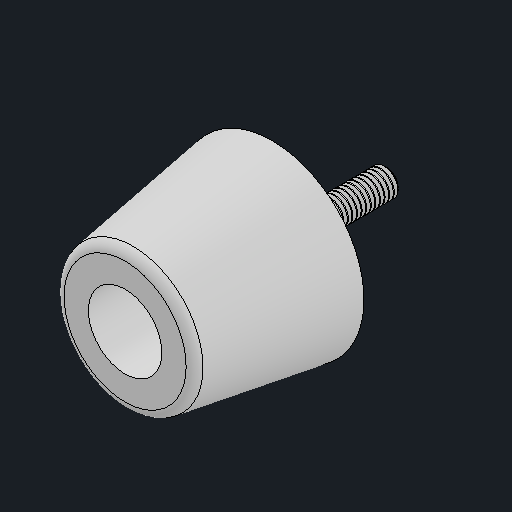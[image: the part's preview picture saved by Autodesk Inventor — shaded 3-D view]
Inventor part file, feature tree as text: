
AUTODESK INVENTOR PART (.ipt)
format: ipt  version: 2024.2 (Build 282272000, 272)  size: 256,000 bytes
history: native  units: mm
features: other x5, fillet x1
ambient origin geometry x8: Origin, YZ Plane, XZ Plane, XY Plane, X Axis, Y Axis, Z Axis, Center Point
bodies: Body1 (feature_tree), Body2 (feature_tree), Body3 (feature_tree)
feature tree (6):
  other  "솔리드1"
  other  "솔리드2"
  other  "솔리드3"
  fillet  "Fillet1"  [1 undecoded]
  other  "Boss-Extrude1"
  other  "_shcs-M3-ndr_-_ThdSchPat_"
note: 1 required parameter value undecoded (feature->parameter linkage not recoverable at this tier; creation-order binding heuristic only, values carry confidence <= 0.55)
